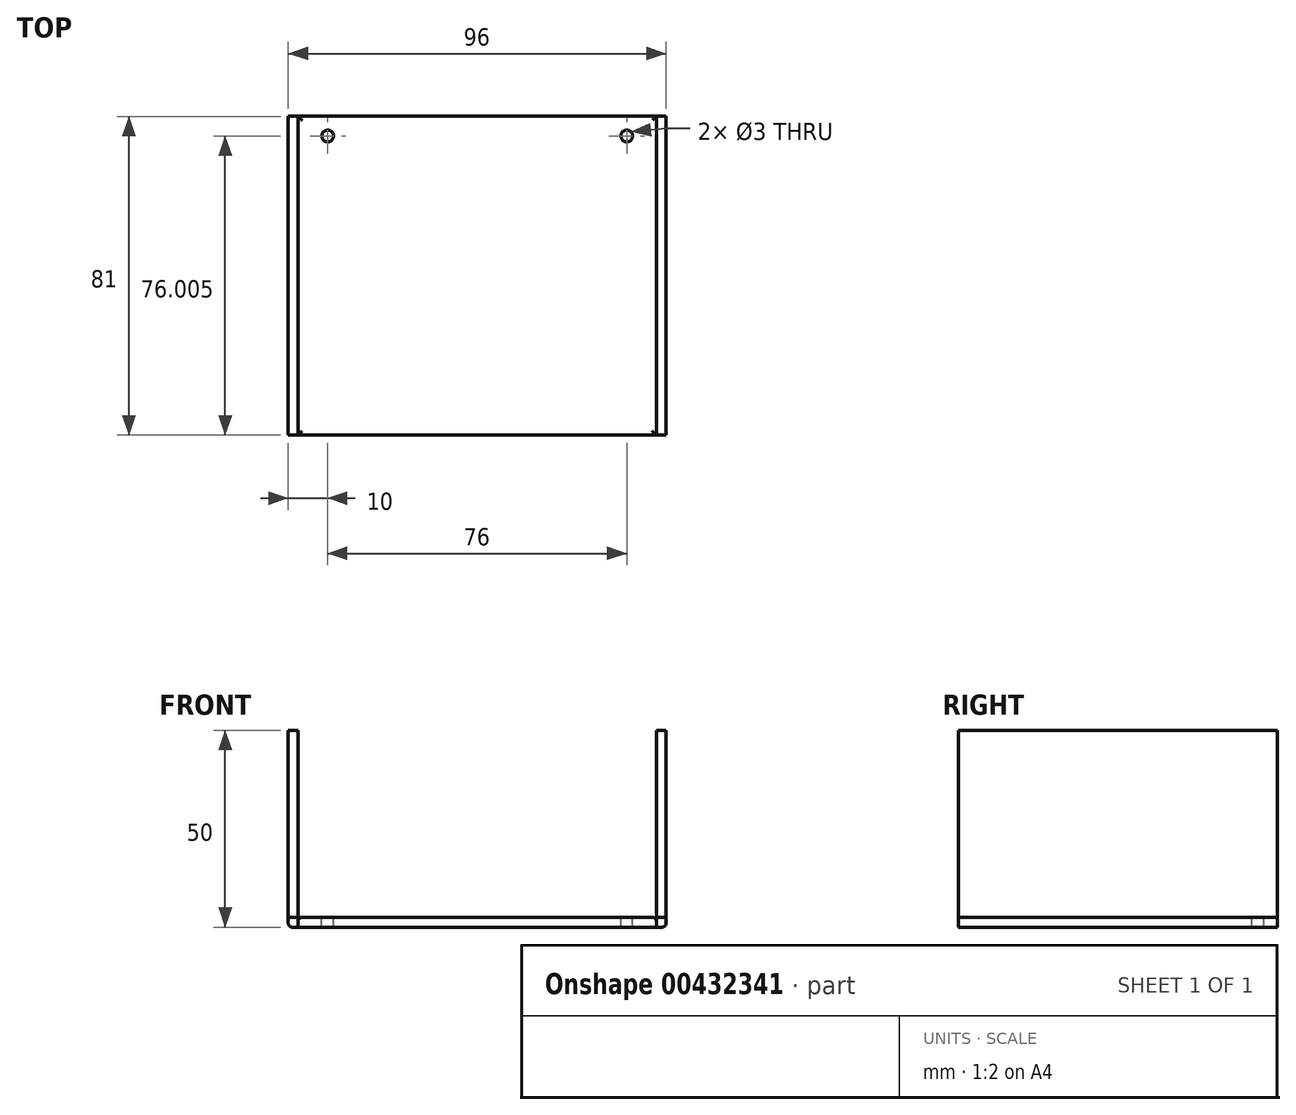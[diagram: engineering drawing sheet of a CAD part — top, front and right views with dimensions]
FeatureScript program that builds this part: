
annotation { "Feature Type Name" : "Feature", "Feature Type Description" : "" }
export const myFeature = defineFeature(function(context is Context, id is Id, definition is map)
    precondition{}
    {
        {
            var Q0;
            Q0=qCreatedBy(makeId("Top.planeOp"),FACE);
            var sketch = newSketch(context, id + "F0", { "sketchPlane" : qUnion([Q0])});
            skLineSegment(sketch, "E0.bottom", {"start": v(-41.49, 60.16) * mm, "end": v(49.51, 60.16) * mm});
            skLineSegment(sketch, "E0.top", {"start": v(-41.49, -20.84) * mm, "end": v(49.51, -20.84) * mm});
            skLineSegment(sketch, "E0.left", {"start": v(-41.49, 60.16) * mm, "end": v(-41.49, -20.84) * mm});
            skLineSegment(sketch, "E0.right", {"start": v(49.51, 60.16) * mm, "end": v(49.51, -20.84) * mm});
            skSolve(sketch);
        }
        {
            var Q0;
            Q0=makeQuery(id+"F0.imprint","IMPRINT",FACE,{"disambiguationData":[TD([[makeQuery(id+"F0.imprint","IMPRINT",EDGE,{"derivedFrom":sQuery(id+"F0.wireOp",EDGE,"E0.bottom")}),-1.0]])]});
            extrude(context, id + "F1", {"entities" : qUnion([Q0]), "depth" : 2.5 * mm});
        }
        {
            var Q0;
            Q0=makeQuery(id+"F1.opExtrude","SWEPT_FACE",FACE,{"disambiguationData":[OSD([sQuery(id+"F0.wireOp",EDGE,"E0.left")])]});
            var sketch = newSketch(context, id + "F2", { "sketchPlane" : qUnion([Q0])});
            skLineSegment(sketch, "E1.bottom", {"start": v(-60.16, 0) * mm, "end": v(20.84, 0) * mm});
            skLineSegment(sketch, "E1.top", {"start": v(-60.16, 50) * mm, "end": v(20.84, 50) * mm});
            skLineSegment(sketch, "E1.left", {"start": v(-60.16, 0) * mm, "end": v(-60.16, 50) * mm});
            skLineSegment(sketch, "E1.right", {"start": v(20.84, 0) * mm, "end": v(20.84, 50) * mm});
            skSolve(sketch);
        }
        {
            var Q0;
            {var subQ0=sQuery(id+"F2.wireOp",EDGE,"E1.top");Q0=makeQuery(id+"F2.imprint","IMPRINT",FACE,{"disambiguationData":[TD([[makeQuery(id+"F2.imprint","IMPRINT",EDGE,{"derivedFrom":subQ0}),-1.0]])]});}
            extrude(context, id + "F3", {"entities" : qUnion([Q0]), "depth" : 2.5 * mm});
        }
        {
            var Q0;
            Q0=makeQuery(id+"F1.opExtrude","SWEPT_FACE",FACE,{"disambiguationData":[OSD([sQuery(id+"F0.wireOp",EDGE,"E0.right")])]});
            var sketch = newSketch(context, id + "F4", { "sketchPlane" : qUnion([Q0])});
            skLineSegment(sketch, "E2.bottom", {"start": v(-20.84, 0) * mm, "end": v(60.16, 0) * mm});
            skLineSegment(sketch, "E2.top", {"start": v(-20.84, 50) * mm, "end": v(60.16, 50) * mm});
            skLineSegment(sketch, "E2.left", {"start": v(-20.84, 0) * mm, "end": v(-20.84, 50) * mm});
            skLineSegment(sketch, "E2.right", {"start": v(60.16, 0) * mm, "end": v(60.16, 50) * mm});
            skSolve(sketch);
        }
        {
            var Q0;
            {var subQ0=sQuery(id+"F4.wireOp",EDGE,"E2.top");Q0=makeQuery(id+"F4.imprint","IMPRINT",FACE,{"disambiguationData":[TD([[makeQuery(id+"F4.imprint","IMPRINT",EDGE,{"derivedFrom":subQ0}),-1.0]])]});}
            extrude(context, id + "F5", {"entities" : qUnion([Q0]), "depth" : 2.5 * mm});
        }
        {
            var Q0;
            Q0=makeQuery(id+"F1.opExtrude","SWEPT_FACE",FACE,{"disambiguationData":[OSD([sQuery(id+"F0.wireOp",EDGE,"E0.right")])]});
            extrude(context, id + "F6", {"entities" : qUnion([Q0]), "depth" : 2.5 * mm});
        }
        {
            var Q0;
            Q0=makeQuery(id+"F1.opExtrude","SWEPT_FACE",FACE,{"disambiguationData":[OSD([sQuery(id+"F0.wireOp",EDGE,"E0.left")])]});
            extrude(context, id + "F7", {"entities" : qUnion([Q0]), "depth" : 2.5 * mm});
        }
        {
            var Q0;
            {var subQ0=sQuery(id+"F0.wireOp",EDGE,"E0.left");Q0=makeQuery(id+"F7.opExtrude","CAP_EDGE",EDGE,{"disambiguationData":[OSD([subQ0]),TDD([makeQuery(id+"F1.opExtrude","CAP_EDGE",EDGE,{"disambiguationData":[OSD([subQ0])],"isStart":true})])],"isStart":false});}
            fillet(context, id + "F8", {"entities" : qUnion([Q0]), "radius" : 1 * mm, "tangentPropagation" : true, "allowEdgeOverflow" : false});
        }
        {
            var Q0;
            {var subQ0=sQuery(id+"F0.wireOp",EDGE,"E0.right");Q0=makeQuery(id+"F6.opExtrude","CAP_EDGE",EDGE,{"disambiguationData":[OSD([subQ0]),TDD([makeQuery(id+"F1.opExtrude","CAP_EDGE",EDGE,{"disambiguationData":[OSD([subQ0])],"isStart":true})])],"isStart":false});}
            var Q1;
            Q1=makeQuery(id+"F1.opExtrude","CAP_FACE",FACE,{"disambiguationData":[OSD([sQuery(id+"F0.wireOp",EDGE,"E0.bottom"),sQuery(id+"F0.wireOp",EDGE,"E0.top"),sQuery(id+"F0.wireOp",EDGE,"E0.left"),sQuery(id+"F0.wireOp",EDGE,"E0.right")])],"isStart":false});
            fillet(context, id + "F9", {"entities" : qUnion([Q0, Q1]), "radius" : 1 * mm, "tangentPropagation" : true, "allowEdgeOverflow" : false});
        }
        {
            var Q0;
            Q0=makeQuery(id+"F1.opExtrude","CAP_FACE",FACE,{"disambiguationData":[OSD([sQuery(id+"F0.wireOp",EDGE,"E0.bottom"),sQuery(id+"F0.wireOp",EDGE,"E0.top"),sQuery(id+"F0.wireOp",EDGE,"E0.left"),sQuery(id+"F0.wireOp",EDGE,"E0.right")])],"isStart":false});
            var sketch = newSketch(context, id + "F10", { "sketchPlane" : qUnion([Q0])});
            skCircle(sketch, "E3", {"center": v(-33.99, 55.16) * mm, "radius": 1.5 * mm});
            skCircle(sketch, "E4", {"center": v(42.01, 55.16) * mm, "radius": 1.5 * mm});
            skSolve(sketch);
        }
        {
            var Q0;
            Q0=makeQuery(id+"F10.imprint","IMPRINT",FACE,{"disambiguationData":[TD([[makeQuery(id+"F10.imprint","IMPRINT",EDGE,{"derivedFrom":sQuery(id+"F10.wireOp",EDGE,"E3")}),1.0]])]});
            var Q1;
            Q1=makeQuery(id+"F10.imprint","IMPRINT",FACE,{"disambiguationData":[TD([[makeQuery(id+"F10.imprint","IMPRINT",EDGE,{"derivedFrom":sQuery(id+"F10.wireOp",EDGE,"E4")}),1.0]])]});
            extrude(context, id + "F11", {"entities" : qUnion([Q0, Q1]), "operationType" : NewBodyOperationType.REMOVE, "oppositeDirection" : true, "depth" : 2.5 * mm});
        }
    });
